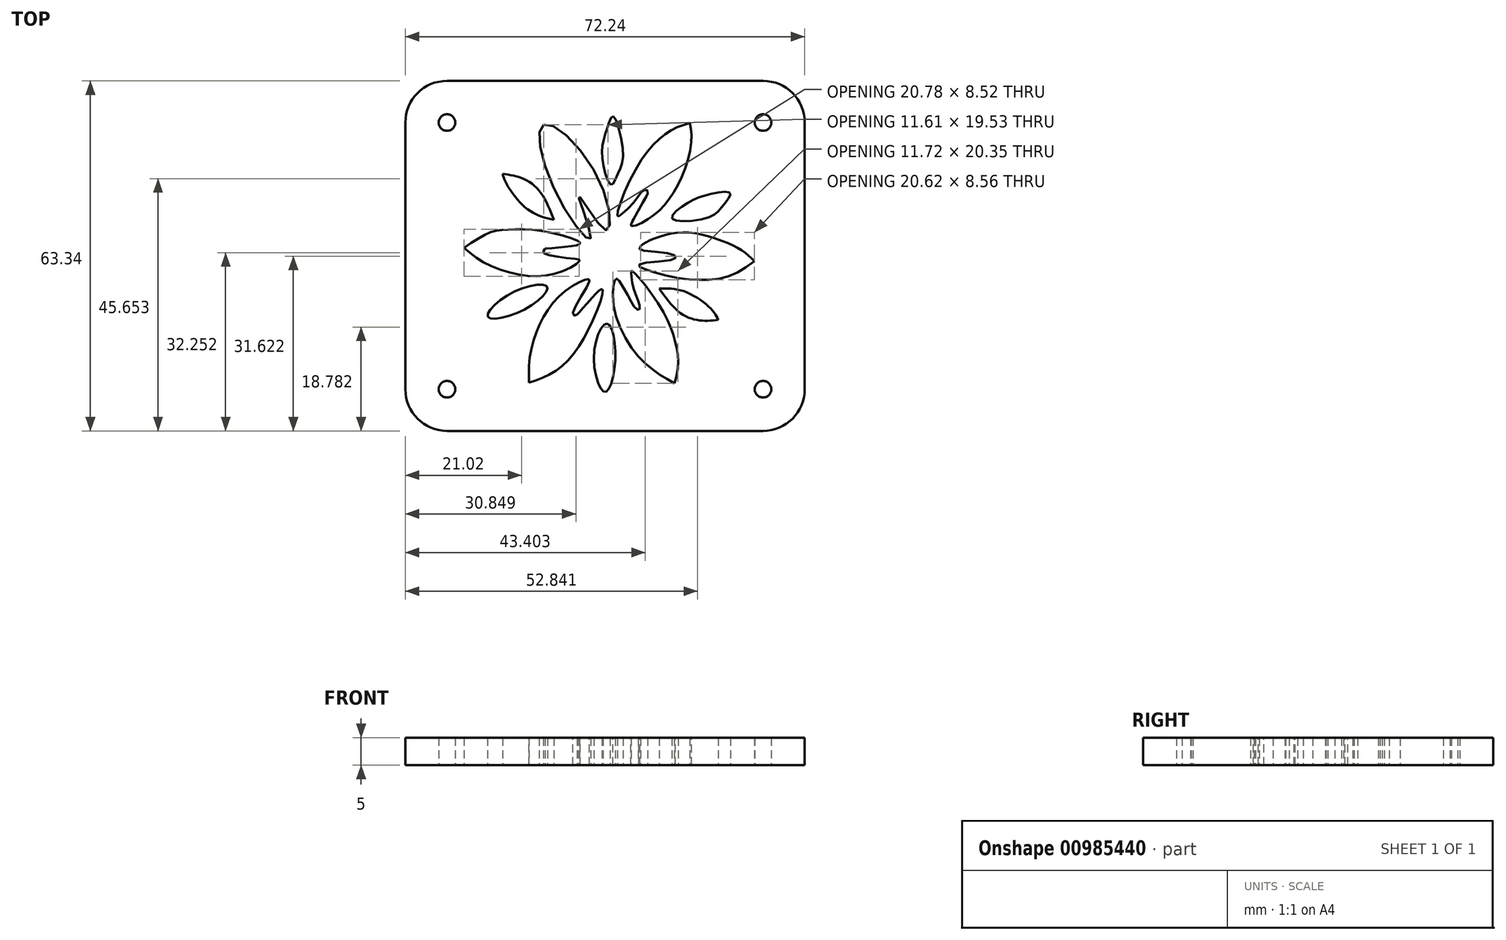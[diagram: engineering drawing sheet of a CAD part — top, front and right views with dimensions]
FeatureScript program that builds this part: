
annotation { "Feature Type Name" : "Feature", "Feature Type Description" : "" }
export const myFeature = defineFeature(function(context is Context, id is Id, definition is map)
    precondition{}
    {
        {
            var Q0;
            Q0=qCreatedBy(makeId("Top.planeOp"),FACE);
            var sketch = newSketch(context, id + "F0", { "sketchPlane" : qUnion([Q0])});
            skLineSegment(sketch, "E0.bottom", {"start": v(28.57, 31.67) * mm, "end": v(-28.58, 31.67) * mm});
            skLineSegment(sketch, "E0.top", {"start": v(28.58, -31.67) * mm, "end": v(-28.57, -31.67) * mm});
            skLineSegment(sketch, "E0.left", {"start": v(36.11, 24.13) * mm, "end": v(36.12, -24.13) * mm});
            skLineSegment(sketch, "E0.right", {"start": v(-36.12, 24.13) * mm, "end": v(-36.11, -24.13) * mm});
            skPoint(sketch, "E0.middle", {"position": v(0, 0) * mm});
            skPoint(sketch, "E1.visualSharp", {"position": v(-36.12, 31.67) * mm});
            skArc(sketch, "E1.filletArc", {"start": v(-28.58, 31.67) * mm, "mid": v(-33.9, 29.46) * mm, "end": v(-36.12, 24.13) * mm});
            skPoint(sketch, "E2.visualSharp", {"position": v(36.11, 31.67) * mm});
            skArc(sketch, "E2.filletArc", {"start": v(36.11, 24.13) * mm, "mid": v(33.9, 29.46) * mm, "end": v(28.57, 31.67) * mm});
            skPoint(sketch, "E3.visualSharp", {"position": v(36.12, -31.67) * mm});
            skArc(sketch, "E3.filletArc", {"start": v(28.58, -31.67) * mm, "mid": v(33.9, -29.46) * mm, "end": v(36.12, -24.13) * mm});
            skPoint(sketch, "E4.visualSharp", {"position": v(-36.11, -31.67) * mm});
            skArc(sketch, "E4.filletArc", {"start": v(-36.11, -24.13) * mm, "mid": v(-33.9, -29.46) * mm, "end": v(-28.57, -31.67) * mm});
            skCircle(sketch, "E5", {"center": v(-28.58, 24.13) * mm, "radius": 1.5 * mm});
            skCircle(sketch, "E6.MirrorC", {"center": v(28.58, 24.13) * mm, "radius": 1.5 * mm});
            skCircle(sketch, "E7.MirrorC", {"center": v(28.58, -24.13) * mm, "radius": 1.5 * mm});
            skCircle(sketch, "E8.MirrorC", {"center": v(-28.58, -24.13) * mm, "radius": 1.5 * mm});
            skFitSpline(sketch, "E9", {"points": [v(-11.08, 23.75) * mm, v(-1, 13.53) * mm, v(0, 4.7) * mm, v(-4.78, 10.88) * mm, v(-2.58, 3.31) * mm, v(-8.75, 11.17) * mm, v(-11.08, 23.75) * mm]});
            skFitSpline(sketch, "E10", {"points": [v(1.49, 25.26) * mm, v(3.24, 18.58) * mm, v(2.3, 14.85) * mm, v(1.12, 12.88) * mm, v(-0.3, 16.44) * mm, v(-0.36, 20.52) * mm, v(0.71, 24.02) * mm, v(1.49, 25.26) * mm]});
            skFitSpline(sketch, "E11", {"points": [v(12.12, 6.74) * mm, v(14.52, 9.33) * mm, v(18.95, 11.17) * mm, v(22.65, 11.36) * mm, v(21.35, 9.14) * mm, v(18.58, 6.93) * mm, v(12.12, 6.74) * mm]});
            skFitSpline(sketch, "E12", {"points": [v(6.41, 1.76) * mm, v(6.22, 1.37) * mm, v(6.54, 1.04) * mm, v(12.18, 0.32) * mm, v(12.73, -0.26) * mm, v(12.43, -0.62) * mm, v(6.66, -1.36) * mm, v(6.11, -1.74) * mm, v(6.83, -2.26) * mm, v(12.48, -3.86) * mm, v(18.03, -4.32) * mm, v(22.72, -3.58) * mm, v(27.03, -0.99) * mm], "startDerivative": vector(-7.7, -11.4) * mm, "endDerivative": vector(34.77, 25.22) * mm});
            skFitSpline(sketch, "E13", {"points": [v(6.41, 1.76) * mm, v(7.94, 2.74) * mm, v(11.73, 3.98) * mm, v(16.43, 4.08) * mm, v(22.4, 2.21) * mm, v(25.32, 0.58) * mm, v(27.03, -0.99) * mm], "startDerivative": vector(11.12, 8.24) * mm, "endDerivative": vector(12.03, -12.1) * mm});
            skFitSpline(sketch, "E14", {"points": [v(7.69, 11.23) * mm, v(7.59, 11.91) * mm, v(6.77, 11.72) * mm, v(5.47, 9.99) * mm, v(2.76, 7.38) * mm, v(2.33, 7.15) * mm, v(2.27, 7.8) * mm, v(5.34, 15.31) * mm, v(9.4, 20.78) * mm, v(12.41, 22.97) * mm, v(15.35, 24.08) * mm], "startDerivative": vector(1.37, 16.48) * mm, "endDerivative": vector(26.64, 8.5) * mm});
            skFitSpline(sketch, "E15", {"points": [v(7.69, 11.23) * mm, v(7.28, 10.48) * mm, v(4.83, 6) * mm, v(4.7, 5.48) * mm, v(5.23, 5.42) * mm, v(7.69, 6.6) * mm, v(10.38, 8.75) * mm, v(12.67, 11.95) * mm, v(14.9, 16.98) * mm, v(15.64, 21.58) * mm, v(15.35, 24.08) * mm], "startDerivative": vector(-4.67, -8.78) * mm, "endDerivative": vector(-4.39, 23.64) * mm});
            skFitSpline(sketch, "E16", {"points": [v(-9.25, 6.51) * mm, v(-11.93, 11.8) * mm, v(-15.26, 14.16) * mm, v(-18.53, 14.82) * mm], "startDerivative": vector(-5.98, 15.07) * mm, "endDerivative": vector(-11.25, 1.35) * mm});
            skFitSpline(sketch, "E17", {"points": [v(-18.53, 14.82) * mm, v(-18.06, 13.5) * mm, v(-15.61, 9.93) * mm, v(-12.5, 7.52) * mm, v(-9.25, 6.51) * mm], "startDerivative": vector(1.82, -6.94) * mm, "endDerivative": vector(12.82, -2.99) * mm});
            skFitSpline(sketch, "E18", {"points": [v(-5.08, -10.6) * mm, v(-5.58, -10.78) * mm, v(-5.77, -10.14) * mm, v(-2.95, -4.92) * mm, v(-2.9, -4.23) * mm, v(-3.7, -4.36) * mm, v(-6.88, -6.12) * mm, v(-10.2, -9.58) * mm, v(-12.37, -13.65) * mm, v(-13.6, -18.25) * mm, v(-13.79, -22.95) * mm], "startDerivative": vector(-12.12, -7.22) * mm, "endDerivative": vector(0.16, -35.41) * mm});
            skFitSpline(sketch, "E19", {"points": [v(-5.08, -10.6) * mm, v(-4.25, -9.72) * mm, v(-1.98, -7.17) * mm, v(-0.95, -6.16) * mm, v(-0.53, -6.03) * mm, v(-0.39, -6.45) * mm, v(-2.37, -12) * mm, v(-6.1, -18.21) * mm, v(-9.83, -21.38) * mm, v(-13.79, -22.95) * mm], "startDerivative": vector(9.32, 9.82) * mm, "endDerivative": vector(-29.18, -9.42) * mm});
            skFitSpline(sketch, "E20", {"points": [v(-21.17, -10.98) * mm, v(-16.75, -6.63) * mm, v(-10.46, -5.62) * mm, v(-14.8, -9.81) * mm, v(-21.17, -10.98) * mm]});
            skFitSpline(sketch, "E21", {"points": [v(0.33, -12.25) * mm, v(-2.02, -17.96) * mm, v(0, -24.62) * mm, v(1.86, -18.41) * mm, v(0.33, -12.25) * mm]});
            skFitSpline(sketch, "E22", {"points": [v(9.77, -5.92) * mm, v(13.65, -10.35) * mm, v(17.25, -11.69) * mm, v(20.49, -11.6) * mm], "startDerivative": vector(9.43, -13.03) * mm, "endDerivative": vector(10.97, 1.07) * mm});
            skFitSpline(sketch, "E23", {"points": [v(9.77, -5.92) * mm, v(14.2, -6.38) * mm, v(19.15, -9.56) * mm, v(20.49, -11.6) * mm], "startDerivative": vector(12.34, 0.36) * mm, "endDerivative": vector(3.72, -7.54) * mm});
            skFitSpline(sketch, "E24", {"points": [v(-10.86, 1.3) * mm, v(-11.18, 0.7) * mm, v(-10.55, 0.23) * mm, v(-5.52, -0.51) * mm, v(-4.59, -0.73) * mm, v(-5, -1.33) * mm, v(-9.28, -3.26) * mm, v(-15.1, -3.48) * mm, v(-21.5, -1.42) * mm, v(-25.5, 1.44) * mm], "startDerivative": vector(-9.02, -11.73) * mm, "endDerivative": vector(-24.76, 20.81) * mm});
            skFitSpline(sketch, "E25", {"points": [v(-10.86, 1.3) * mm, v(-6.97, 1.64) * mm, v(-4.73, 2.06) * mm, v(-4.5, 2.34) * mm, v(-4.91, 2.73) * mm, v(-12.18, 4.62) * mm, v(-17.91, 4.74) * mm, v(-20.89, 4.2) * mm, v(-25.5, 1.44) * mm], "startDerivative": vector(28.23, 2.28) * mm, "endDerivative": vector(-29.43, -20.3) * mm});
            skFitSpline(sketch, "E26", {"points": [v(6.01, -8.14) * mm, v(6.28, -9.28) * mm, v(6.16, -9.77) * mm, v(5.47, -9.44) * mm, v(4.32, -7.54) * mm, v(2.44, -4.39) * mm, v(2.08, -4.12) * mm, v(1.72, -4.58) * mm, v(1.56, -9.02) * mm, v(4.58, -16.34) * mm, v(8.89, -20.78) * mm, v(12.55, -23.06) * mm], "startDerivative": vector(5.47, -18.75) * mm, "endDerivative": vector(29.66, -16.72) * mm});
            skFitSpline(sketch, "E27", {"points": [v(6.01, -8.14) * mm, v(4.97, -5.1) * mm, v(4.7, -3.15) * mm, v(4.77, -2.69) * mm, v(6.01, -3.8) * mm, v(10.72, -10.46) * mm, v(12.48, -14.84) * mm, v(13.2, -18.3) * mm, v(13, -21.37) * mm, v(12.55, -23.06) * mm], "startDerivative": vector(-10.4, 26.26) * mm, "endDerivative": vector(-5.64, -17.83) * mm});
            skSolve(sketch);
        }
        {
            var Q0;
            Q0=makeQuery(id+"F0.imprint","IMPRINT",FACE,{"disambiguationData":[TD([[makeQuery(id+"F0.imprint","IMPRINT",EDGE,{"derivedFrom":sQuery(id+"F0.wireOp",EDGE,"E0.bottom")}),1.0]])]});
            extrude(context, id + "F1", {"entities" : qUnion([Q0]), "depth" : 5 * mm, "offsetDistance" : 25 * mm});
        }
    });
